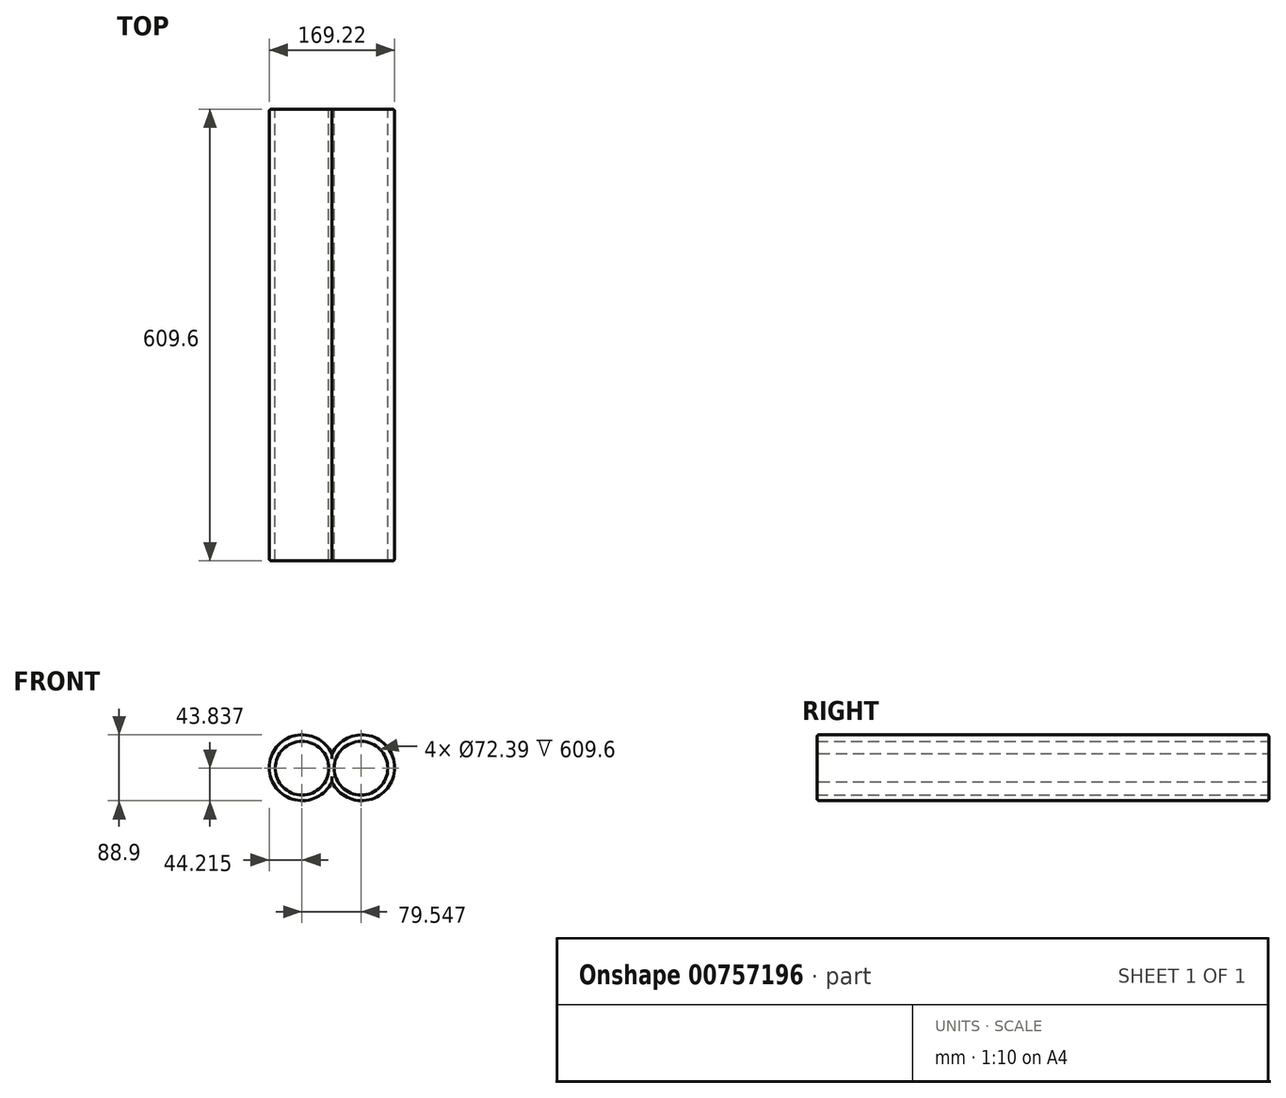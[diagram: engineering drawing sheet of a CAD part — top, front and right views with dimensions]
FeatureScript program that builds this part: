
annotation { "Feature Type Name" : "Feature", "Feature Type Description" : "" }
export const myFeature = defineFeature(function(context is Context, id is Id, definition is map)
    precondition{}
    {
        {
            var Q0;
            Q0=qCreatedBy(makeId("Front.planeOp"),FACE);
            var sketch = newSketch(context, id + "F0", { "sketchPlane" : qUnion([Q0])});
            skArc(sketch, "E0", {"start": v(0, 38.1) * mm, "mid": v(-84.61, 19.05) * mm, "end": v(0, 0) * mm});
            skArc(sketch, "E1", {"start": v(0, 0) * mm, "mid": v(84.61, 19.05) * mm, "end": v(0, 38.1) * mm});
            skSolve(sketch);
        }
        {
            var Q0;
            Q0 = qSketchRegion(id + "F0", true);
            extrude(context, id + "F1", {"entities" : qUnion([Q0]), "depth" : 609.6 * mm, "offsetDistance" : 25.4 * mm});
        }
        {
            var Q0;
            Q0=qCreatedBy(makeId("Front.planeOp"),FACE);
            var sketch = newSketch(context, id + "F2", { "sketchPlane" : qUnion([Q0])});
            skLineSegment(sketch, "E2", {"start": v(0, 0) * mm, "end": v(0, 36.87) * mm, "construction": true});
            skLineSegment(sketch, "E3", {"start": v(0, 36.87) * mm, "end": v(0, 18.44) * mm, "construction": true});
            skLineSegment(sketch, "E4", {"start": v(0, 18.44) * mm, "end": v(39.15, 18.44) * mm, "construction": true});
            skLineSegment(sketch, "E5", {"start": v(39.15, 18.44) * mm, "end": v(-40.4, 18.44) * mm, "construction": true});
            skLineSegment(sketch, "E6", {"start": v(-40.4, 18.44) * mm, "end": v(0, 18.44) * mm, "construction": true});
            skCircle(sketch, "E7", {"center": v(-40.4, 18.44) * mm, "radius": 36.2 * mm});
            skCircle(sketch, "E8", {"center": v(39.15, 18.44) * mm, "radius": 36.2 * mm});
            skSolve(sketch);
        }
        {
            var Q0;
            Q0 = qSketchRegion(id + "F2", true);
            extrude(context, id + "F3", {"entities" : qUnion([Q0]), "operationType" : NewBodyOperationType.REMOVE, "depth" : 609.6 * mm, "offsetDistance" : 25.4 * mm});
        }
        {
            var Q0;
            Q0=makeQuery(id+"F3.boolean.opBoolean","COPY",EDGE,{"derivedFrom":makeQuery(id+"F3.opExtrude","CAP_EDGE",EDGE,{"disambiguationData":[OSD([sQuery(id+"F2.wireOp",EDGE,"E7")])],"isStart":false})});
            var Q1;
            Q1=makeQuery(id+"F3.boolean.opBoolean","COPY",EDGE,{"derivedFrom":makeQuery(id+"F3.opExtrude","CAP_EDGE",EDGE,{"disambiguationData":[OSD([sQuery(id+"F2.wireOp",EDGE,"E8")])],"isStart":false})});
            var Q2;
            Q2=makeQuery(id+"F3.boolean.opBoolean","COPY",EDGE,{"derivedFrom":makeQuery(id+"F3.opExtrude","CAP_EDGE",EDGE,{"disambiguationData":[OSD([sQuery(id+"F2.wireOp",EDGE,"E8")])],"isStart":true})});
            var Q3;
            Q3=makeQuery(id+"F3.boolean.opBoolean","COPY",EDGE,{"derivedFrom":makeQuery(id+"F3.opExtrude","CAP_EDGE",EDGE,{"disambiguationData":[OSD([sQuery(id+"F2.wireOp",EDGE,"E7")])],"isStart":true})});
            var Q4;
            Q4=makeQuery(id+"F1.opExtrude","CAP_EDGE",EDGE,{"disambiguationData":[OSD([sQuery(id+"F0.wireOp",EDGE,"E1")])],"isStart":true});
            var Q5;
            Q5=makeQuery(id+"F1.opExtrude","CAP_EDGE",EDGE,{"disambiguationData":[OSD([sQuery(id+"F0.wireOp",EDGE,"E0")])],"isStart":true});
            var Q6;
            Q6=makeQuery(id+"F1.opExtrude","CAP_EDGE",EDGE,{"disambiguationData":[OSD([sQuery(id+"F0.wireOp",EDGE,"E1")])],"isStart":false});
            var Q7;
            Q7=makeQuery(id+"F1.opExtrude","CAP_EDGE",EDGE,{"disambiguationData":[OSD([sQuery(id+"F0.wireOp",EDGE,"E0")])],"isStart":false});
            fillet(context, id + "F4", {"entities" : qUnion([Q0, Q1, Q2, Q3, Q4, Q5, Q6, Q7]), "radius" : 2.54 * mm, "tangentPropagation" : true, "allowEdgeOverflow" : false});
        }
    });
